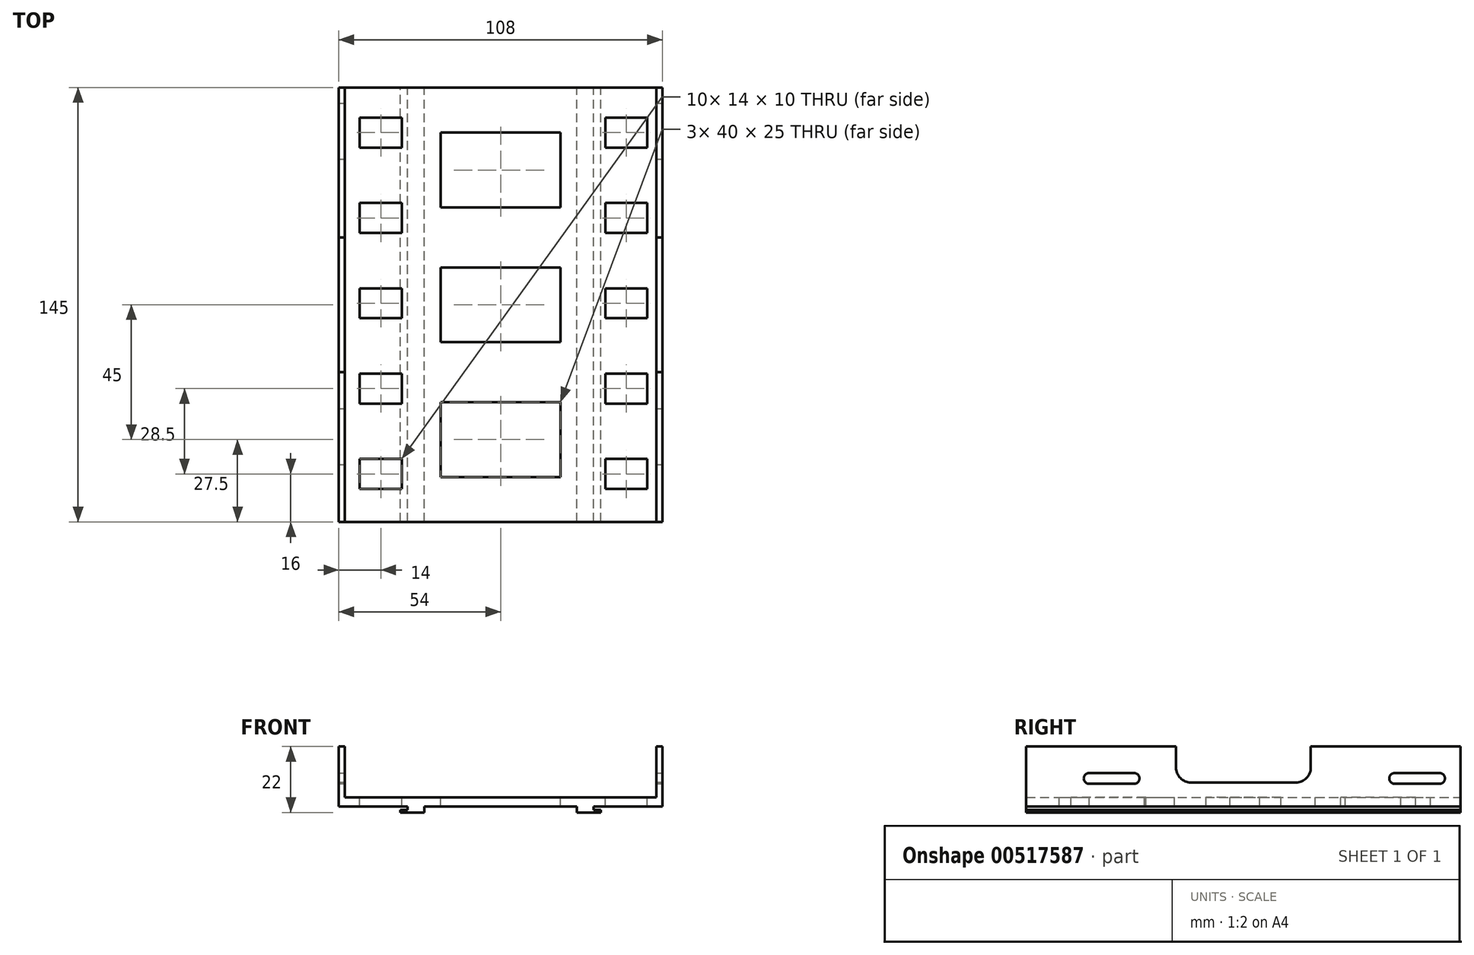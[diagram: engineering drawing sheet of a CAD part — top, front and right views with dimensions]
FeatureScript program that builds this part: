
annotation { "Feature Type Name" : "Feature", "Feature Type Description" : "" }
export const myFeature = defineFeature(function(context is Context, id is Id, definition is map)
    precondition{}
    {
        {
            var Q0;
            Q0=qCreatedBy(makeId("Front.planeOp"),FACE);
            var sketch = newSketch(context, id + "F0", { "sketchPlane" : qUnion([Q0])});
            skLineSegment(sketch, "E0", {"start": v(-54, 0) * mm, "end": v(-31, 0) * mm});
            skLineSegment(sketch, "E1", {"start": v(-54, 0) * mm, "end": v(-54, 20) * mm});
            skLineSegment(sketch, "E2", {"start": v(-54, 20) * mm, "end": v(-52, 20) * mm});
            skLineSegment(sketch, "E3", {"start": v(-52, 20) * mm, "end": v(-52, 3) * mm});
            skLineSegment(sketch, "E4", {"start": v(-52, 3) * mm, "end": v(0, 3) * mm});
            skLineSegment(sketch, "E5", {"start": v(0, 56.91) * mm, "end": v(0, -44.98) * mm, "construction": true});
            skLineSegment(sketch, "E6", {"start": v(-31, 0) * mm, "end": v(-31, -1.15) * mm});
            skLineSegment(sketch, "E7", {"start": v(-31, -1.15) * mm, "end": v(-33.5, -1.15) * mm});
            skLineSegment(sketch, "E8", {"start": v(-33.5, -1.15) * mm, "end": v(-33.5, -2) * mm});
            skLineSegment(sketch, "E9", {"start": v(-33.5, -2) * mm, "end": v(-25.5, -2) * mm});
            skLineSegment(sketch, "E10.MirrorCS", {"start": v(54, 20) * mm, "end": v(52, 20) * mm});
            skLineSegment(sketch, "E11.MirrorCS", {"start": v(31, 0) * mm, "end": v(31, -1.15) * mm});
            skLineSegment(sketch, "E12.MirrorCS", {"start": v(33.5, -1.15) * mm, "end": v(33.5, -2) * mm});
            skLineSegment(sketch, "E13.MirrorCS", {"start": v(54, 0) * mm, "end": v(31, 0) * mm});
            skLineSegment(sketch, "E14.MirrorCS", {"start": v(54, 0) * mm, "end": v(54, 20) * mm});
            skLineSegment(sketch, "E15.MirrorCS", {"start": v(31, -1.15) * mm, "end": v(33.5, -1.15) * mm});
            skLineSegment(sketch, "E16.MirrorCS", {"start": v(52, 20) * mm, "end": v(52, 3) * mm});
            skLineSegment(sketch, "E17.MirrorCS", {"start": v(33.5, -2) * mm, "end": v(25.5, -2) * mm});
            skLineSegment(sketch, "E18.MirrorCS", {"start": v(52, 3) * mm, "end": v(0, 3) * mm});
            skLineSegment(sketch, "E19.top", {"start": v(-25.5, 0) * mm, "end": v(25.5, 0) * mm});
            skLineSegment(sketch, "E19.left", {"start": v(-25.5, -2) * mm, "end": v(-25.5, 0) * mm});
            skLineSegment(sketch, "E19.right", {"start": v(25.5, -2) * mm, "end": v(25.5, 0) * mm});
            skPoint(sketch, "E20.orphan", {"position": v(0, -2) * mm});
            skSolve(sketch);
        }
        {
            var Q0;
            Q0=makeQuery(id+"F0.imprint","IMPRINT",FACE,{"disambiguationData":[TD([[makeQuery(id+"F0.imprint","IMPRINT",EDGE,{"derivedFrom":sQuery(id+"F0.wireOp",EDGE,"E0")}),1.0]])]});
            extrude(context, id + "F1", {"entities" : qUnion([Q0]), "depth" : 145 * mm, "offsetDistance" : 25 * mm});
        }
        {
            var Q0;
            Q0=makeQuery(id+"F1.opExtrude","SWEPT_FACE",FACE,{"disambiguationData":[OSD([sQuery(id+"F0.wireOp",EDGE,"E14.MirrorCS")])]});
            var sketch = newSketch(context, id + "F2", { "sketchPlane" : qUnion([Q0])});
            skLineSegment(sketch, "E21", {"start": v(-160.18, 9.35) * mm, "end": v(-3.18, 9.35) * mm, "construction": true});
            skLineSegment(sketch, "E22", {"start": v(-116.5, -5.07) * mm, "end": v(-116.5, 28.85) * mm, "construction": true});
            skLineSegment(sketch, "E23", {"start": v(-14.5, -7.08) * mm, "end": v(-14.5, 28.85) * mm, "construction": true});
            skArc(sketch, "E24", {"start": v(-124, 11.15) * mm, "mid": v(-125.8, 9.35) * mm, "end": v(-124, 7.55) * mm});
            skArc(sketch, "E25", {"start": v(-109, 7.55) * mm, "mid": v(-107.2, 9.35) * mm, "end": v(-109, 11.15) * mm});
            skLineSegment(sketch, "E26", {"start": v(-124, 11.15) * mm, "end": v(-109, 11.15) * mm});
            skLineSegment(sketch, "E27", {"start": v(-124, 7.55) * mm, "end": v(-109, 7.55) * mm});
            skLineSegment(sketch, "E28.1.0.0", {"start": v(-22, 7.55) * mm, "end": v(-7, 7.55) * mm});
            skArc(sketch, "E28.1.0.1", {"start": v(-22, 11.15) * mm, "mid": v(-23.8, 9.35) * mm, "end": v(-22, 7.55) * mm});
            skArc(sketch, "E28.1.0.2", {"start": v(-7, 7.55) * mm, "mid": v(-5.2, 9.35) * mm, "end": v(-7, 11.15) * mm});
            skLineSegment(sketch, "E28.1.0.3", {"start": v(-22, 11.15) * mm, "end": v(-7, 11.15) * mm});
            skLineSegment(sketch, "E28.direction1", {"start": v(-124, 7.55) * mm, "end": v(-22, 7.55) * mm, "construction": true});
            skSolve(sketch);
        }
        {
            var Q0;
            Q0=makeQuery(id+"F2.imprint","IMPRINT",FACE,{"disambiguationData":[TD([[makeQuery(id+"F2.imprint","IMPRINT",EDGE,{"derivedFrom":sQuery(id+"F2.wireOp",EDGE,"E24")}),1.0]])]});
            var Q1;
            Q1=makeQuery(id+"F2.imprint","IMPRINT",FACE,{"disambiguationData":[TD([[makeQuery(id+"F2.imprint","IMPRINT",EDGE,{"derivedFrom":sQuery(id+"F2.wireOp",EDGE,"E28.1.0.0")}),1.0]])]});
            extrude(context, id + "F3", {"entities" : qUnion([Q0, Q1]), "operationType" : NewBodyOperationType.REMOVE, "endBound" : BoundingType.THROUGH_ALL, "oppositeDirection" : true, "depth" : 25 * mm, "offsetDistance" : 25 * mm});
        }
        {
            var Q0;
            Q0=makeQuery(id+"F1.opExtrude","SWEPT_FACE",FACE,{"disambiguationData":[OSD([sQuery(id+"F0.wireOp",EDGE,"E4"),sQuery(id+"F0.wireOp",EDGE,"E18.MirrorCS")])]});
            var sketch = newSketch(context, id + "F4", { "sketchPlane" : qUnion([Q0])});
            skLineSegment(sketch, "E29", {"start": v(0, -145) * mm, "end": v(0, 0) * mm, "construction": true});
            skLineSegment(sketch, "E30.bottom", {"start": v(20, -15) * mm, "end": v(-20, -15) * mm});
            skLineSegment(sketch, "E30.top", {"start": v(20, -40) * mm, "end": v(-20, -40) * mm});
            skLineSegment(sketch, "E30.left", {"start": v(20, -15) * mm, "end": v(20, -40) * mm});
            skLineSegment(sketch, "E30.right", {"start": v(-20, -15) * mm, "end": v(-20, -40) * mm});
            skPoint(sketch, "E30.middle", {"position": v(0, -27.5) * mm});
            skLineSegment(sketch, "E31.0.1.0", {"start": v(20, -85) * mm, "end": v(-20, -85) * mm});
            skPoint(sketch, "E31.0.1.1", {"position": v(0, -72.5) * mm});
            skLineSegment(sketch, "E31.0.1.2", {"start": v(20, -60) * mm, "end": v(-20, -60) * mm});
            skLineSegment(sketch, "E31.0.1.3", {"start": v(20, -60) * mm, "end": v(20, -85) * mm});
            skLineSegment(sketch, "E31.0.1.4", {"start": v(-20, -60) * mm, "end": v(-20, -85) * mm});
            skLineSegment(sketch, "E31.0.2.0", {"start": v(20, -130) * mm, "end": v(-20, -130) * mm});
            skPoint(sketch, "E31.0.2.1", {"position": v(0, -117.5) * mm});
            skLineSegment(sketch, "E31.0.2.2", {"start": v(20, -105) * mm, "end": v(-20, -105) * mm});
            skLineSegment(sketch, "E31.0.2.3", {"start": v(20, -105) * mm, "end": v(20, -130) * mm});
            skLineSegment(sketch, "E31.0.2.4", {"start": v(-20, -105) * mm, "end": v(-20, -130) * mm});
            skLineSegment(sketch, "E31.direction1", {"start": v(-20, -40) * mm, "end": v(5, -40) * mm, "construction": true});
            skLineSegment(sketch, "E31.direction2", {"start": v(-20, -40) * mm, "end": v(-20, -85) * mm, "construction": true});
            skLineSegment(sketch, "E32.bottom", {"start": v(49, -20) * mm, "end": v(35, -20) * mm});
            skLineSegment(sketch, "E32.top", {"start": v(49, -10) * mm, "end": v(35, -10) * mm});
            skLineSegment(sketch, "E32.left", {"start": v(49, -20) * mm, "end": v(49, -10) * mm});
            skLineSegment(sketch, "E32.right", {"start": v(35, -20) * mm, "end": v(35, -10) * mm});
            skPoint(sketch, "E32.middle", {"position": v(42, -15) * mm});
            skLineSegment(sketch, "E33.0.1.0", {"start": v(49, -48.5) * mm, "end": v(35, -48.5) * mm});
            skLineSegment(sketch, "E33.0.1.1", {"start": v(35, -48.5) * mm, "end": v(35, -38.5) * mm});
            skPoint(sketch, "E33.0.1.2", {"position": v(42, -43.5) * mm});
            skLineSegment(sketch, "E33.0.1.3", {"start": v(49, -38.5) * mm, "end": v(35, -38.5) * mm});
            skLineSegment(sketch, "E33.0.1.4", {"start": v(49, -48.5) * mm, "end": v(49, -38.5) * mm});
            skLineSegment(sketch, "E33.0.2.0", {"start": v(49, -77) * mm, "end": v(35, -77) * mm});
            skLineSegment(sketch, "E33.0.2.1", {"start": v(35, -77) * mm, "end": v(35, -67) * mm});
            skPoint(sketch, "E33.0.2.2", {"position": v(42, -72) * mm});
            skLineSegment(sketch, "E33.0.2.3", {"start": v(49, -67) * mm, "end": v(35, -67) * mm});
            skLineSegment(sketch, "E33.0.2.4", {"start": v(49, -77) * mm, "end": v(49, -67) * mm});
            skLineSegment(sketch, "E33.0.3.0", {"start": v(49, -105.5) * mm, "end": v(35, -105.5) * mm});
            skLineSegment(sketch, "E33.0.3.1", {"start": v(35, -105.5) * mm, "end": v(35, -95.5) * mm});
            skPoint(sketch, "E33.0.3.2", {"position": v(42, -100.5) * mm});
            skLineSegment(sketch, "E33.0.3.3", {"start": v(49, -95.5) * mm, "end": v(35, -95.5) * mm});
            skLineSegment(sketch, "E33.0.3.4", {"start": v(49, -105.5) * mm, "end": v(49, -95.5) * mm});
            skLineSegment(sketch, "E33.0.4.0", {"start": v(49, -134) * mm, "end": v(35, -134) * mm});
            skLineSegment(sketch, "E33.0.4.1", {"start": v(35, -134) * mm, "end": v(35, -124) * mm});
            skPoint(sketch, "E33.0.4.2", {"position": v(42, -129) * mm});
            skLineSegment(sketch, "E33.0.4.3", {"start": v(49, -124) * mm, "end": v(35, -124) * mm});
            skLineSegment(sketch, "E33.0.4.4", {"start": v(49, -134) * mm, "end": v(49, -124) * mm});
            skLineSegment(sketch, "E33.1.0.0", {"start": v(-33, -20) * mm, "end": v(-47, -20) * mm});
            skLineSegment(sketch, "E33.1.0.1", {"start": v(-47, -20) * mm, "end": v(-47, -10) * mm});
            skPoint(sketch, "E33.1.0.2", {"position": v(-40, -15) * mm});
            skLineSegment(sketch, "E33.1.0.3", {"start": v(-33, -10) * mm, "end": v(-47, -10) * mm});
            skLineSegment(sketch, "E33.1.0.4", {"start": v(-33, -20) * mm, "end": v(-33, -10) * mm});
            skLineSegment(sketch, "E33.1.1.0", {"start": v(-33, -48.5) * mm, "end": v(-47, -48.5) * mm});
            skLineSegment(sketch, "E33.1.1.1", {"start": v(-47, -48.5) * mm, "end": v(-47, -38.5) * mm});
            skPoint(sketch, "E33.1.1.2", {"position": v(-40, -43.5) * mm});
            skLineSegment(sketch, "E33.1.1.3", {"start": v(-33, -38.5) * mm, "end": v(-47, -38.5) * mm});
            skLineSegment(sketch, "E33.1.1.4", {"start": v(-33, -48.5) * mm, "end": v(-33, -38.5) * mm});
            skLineSegment(sketch, "E33.1.2.0", {"start": v(-33, -77) * mm, "end": v(-47, -77) * mm});
            skLineSegment(sketch, "E33.1.2.1", {"start": v(-47, -77) * mm, "end": v(-47, -67) * mm});
            skPoint(sketch, "E33.1.2.2", {"position": v(-40, -72) * mm});
            skLineSegment(sketch, "E33.1.2.3", {"start": v(-33, -67) * mm, "end": v(-47, -67) * mm});
            skLineSegment(sketch, "E33.1.2.4", {"start": v(-33, -77) * mm, "end": v(-33, -67) * mm});
            skLineSegment(sketch, "E33.1.3.0", {"start": v(-33, -105.5) * mm, "end": v(-47, -105.5) * mm});
            skLineSegment(sketch, "E33.1.3.1", {"start": v(-47, -105.5) * mm, "end": v(-47, -95.5) * mm});
            skPoint(sketch, "E33.1.3.2", {"position": v(-40, -100.5) * mm});
            skLineSegment(sketch, "E33.1.3.3", {"start": v(-33, -95.5) * mm, "end": v(-47, -95.5) * mm});
            skLineSegment(sketch, "E33.1.3.4", {"start": v(-33, -105.5) * mm, "end": v(-33, -95.5) * mm});
            skLineSegment(sketch, "E33.1.4.0", {"start": v(-33, -134) * mm, "end": v(-47, -134) * mm});
            skLineSegment(sketch, "E33.1.4.1", {"start": v(-47, -134) * mm, "end": v(-47, -124) * mm});
            skPoint(sketch, "E33.1.4.2", {"position": v(-40, -129) * mm});
            skLineSegment(sketch, "E33.1.4.3", {"start": v(-33, -124) * mm, "end": v(-47, -124) * mm});
            skLineSegment(sketch, "E33.1.4.4", {"start": v(-33, -134) * mm, "end": v(-33, -124) * mm});
            skLineSegment(sketch, "E33.direction1", {"start": v(35, -20) * mm, "end": v(-47, -20) * mm, "construction": true});
            skLineSegment(sketch, "E33.direction2", {"start": v(35, -20) * mm, "end": v(35, -48.5) * mm, "construction": true});
            skSolve(sketch);
        }
        {
            var Q0;
            Q0=makeQuery(id+"F4.imprint","IMPRINT",FACE,{"disambiguationData":[TD([[makeQuery(id+"F4.imprint","IMPRINT",EDGE,{"derivedFrom":sQuery(id+"F4.wireOp",EDGE,"E30.bottom")}),1.0]])]});
            var Q1;
            Q1=makeQuery(id+"F4.imprint","IMPRINT",FACE,{"disambiguationData":[TD([[makeQuery(id+"F4.imprint","IMPRINT",EDGE,{"derivedFrom":sQuery(id+"F4.wireOp",EDGE,"E33.1.0.0")}),-1.0]])]});
            var Q2;
            Q2=makeQuery(id+"F4.imprint","IMPRINT",FACE,{"disambiguationData":[TD([[makeQuery(id+"F4.imprint","IMPRINT",EDGE,{"derivedFrom":sQuery(id+"F4.wireOp",EDGE,"E33.1.1.0")}),-1.0]])]});
            var Q3;
            Q3=makeQuery(id+"F4.imprint","IMPRINT",FACE,{"disambiguationData":[TD([[makeQuery(id+"F4.imprint","IMPRINT",EDGE,{"derivedFrom":sQuery(id+"F4.wireOp",EDGE,"E33.1.2.0")}),-1.0]])]});
            var Q4;
            Q4=makeQuery(id+"F4.imprint","IMPRINT",FACE,{"disambiguationData":[TD([[makeQuery(id+"F4.imprint","IMPRINT",EDGE,{"derivedFrom":sQuery(id+"F4.wireOp",EDGE,"E33.1.3.0")}),-1.0]])]});
            var Q5;
            Q5=makeQuery(id+"F4.imprint","IMPRINT",FACE,{"disambiguationData":[TD([[makeQuery(id+"F4.imprint","IMPRINT",EDGE,{"derivedFrom":sQuery(id+"F4.wireOp",EDGE,"E33.1.4.0")}),-1.0]])]});
            var Q6;
            Q6=makeQuery(id+"F4.imprint","IMPRINT",FACE,{"disambiguationData":[TD([[makeQuery(id+"F4.imprint","IMPRINT",EDGE,{"derivedFrom":sQuery(id+"F4.wireOp",EDGE,"E32.bottom")}),-1.0]])]});
            var Q7;
            Q7=makeQuery(id+"F4.imprint","IMPRINT",FACE,{"disambiguationData":[TD([[makeQuery(id+"F4.imprint","IMPRINT",EDGE,{"derivedFrom":sQuery(id+"F4.wireOp",EDGE,"E33.0.1.0")}),-1.0]])]});
            var Q8;
            Q8=makeQuery(id+"F4.imprint","IMPRINT",FACE,{"disambiguationData":[TD([[makeQuery(id+"F4.imprint","IMPRINT",EDGE,{"derivedFrom":sQuery(id+"F4.wireOp",EDGE,"E33.0.2.0")}),-1.0]])]});
            var Q9;
            Q9=makeQuery(id+"F4.imprint","IMPRINT",FACE,{"disambiguationData":[TD([[makeQuery(id+"F4.imprint","IMPRINT",EDGE,{"derivedFrom":sQuery(id+"F4.wireOp",EDGE,"E33.0.3.0")}),-1.0]])]});
            var Q10;
            Q10=makeQuery(id+"F4.imprint","IMPRINT",FACE,{"disambiguationData":[TD([[makeQuery(id+"F4.imprint","IMPRINT",EDGE,{"derivedFrom":sQuery(id+"F4.wireOp",EDGE,"E33.0.4.0")}),-1.0]])]});
            var Q11;
            Q11=makeQuery(id+"F4.imprint","IMPRINT",FACE,{"disambiguationData":[TD([[makeQuery(id+"F4.imprint","IMPRINT",EDGE,{"derivedFrom":sQuery(id+"F4.wireOp",EDGE,"E31.0.1.0")}),-1.0]])]});
            var Q12;
            Q12=makeQuery(id+"F4.imprint","IMPRINT",FACE,{"disambiguationData":[TD([[makeQuery(id+"F4.imprint","IMPRINT",EDGE,{"derivedFrom":sQuery(id+"F4.wireOp",EDGE,"E31.0.2.0")}),-1.0]])]});
            extrude(context, id + "F5", {"entities" : qUnion([Q0, Q1, Q2, Q3, Q4, Q5, Q6, Q7, Q8, Q9, Q10, Q11, Q12]), "operationType" : NewBodyOperationType.REMOVE, "endBound" : BoundingType.THROUGH_ALL, "oppositeDirection" : true, "depth" : 25 * mm, "offsetDistance" : 25 * mm});
        }
        {
            var Q0;
            Q0=makeQuery(id+"F1.opExtrude","SWEPT_FACE",FACE,{"disambiguationData":[OSD([sQuery(id+"F0.wireOp",EDGE,"E1")])]});
            var sketch = newSketch(context, id + "F6", { "sketchPlane" : qUnion([Q0])});
            skLineSegment(sketch, "E34", {"start": v(72.5, 20) * mm, "end": v(72.5, 0) * mm, "construction": true});
            skLineSegment(sketch, "E35.bottom", {"start": v(50, 20) * mm, "end": v(95, 20) * mm});
            skLineSegment(sketch, "E35.top", {"start": v(55, 8) * mm, "end": v(90, 8) * mm});
            skLineSegment(sketch, "E35.left", {"start": v(50, 20) * mm, "end": v(50, 13) * mm});
            skLineSegment(sketch, "E35.right", {"start": v(95, 20) * mm, "end": v(95, 13) * mm});
            skPoint(sketch, "E36.visualSharp", {"position": v(50, 8) * mm});
            skArc(sketch, "E36.filletArc", {"start": v(50, 13) * mm, "mid": v(51.46, 9.46) * mm, "end": v(55, 8) * mm});
            skPoint(sketch, "E37.visualSharp", {"position": v(95, 8) * mm});
            skArc(sketch, "E37.filletArc", {"start": v(90, 8) * mm, "mid": v(93.54, 9.46) * mm, "end": v(95, 13) * mm});
            skSolve(sketch);
        }
        {
            var Q0;
            Q0=makeQuery(id+"F6.imprint","IMPRINT",FACE,{"disambiguationData":[TD([[makeQuery(id+"F6.imprint","IMPRINT",EDGE,{"derivedFrom":sQuery(id+"F6.wireOp",EDGE,"E35.bottom")}),1.0]])]});
            extrude(context, id + "F7", {"entities" : qUnion([Q0]), "operationType" : NewBodyOperationType.REMOVE, "endBound" : BoundingType.THROUGH_ALL, "oppositeDirection" : true, "depth" : 25 * mm, "offsetDistance" : 25 * mm});
        }
    });
